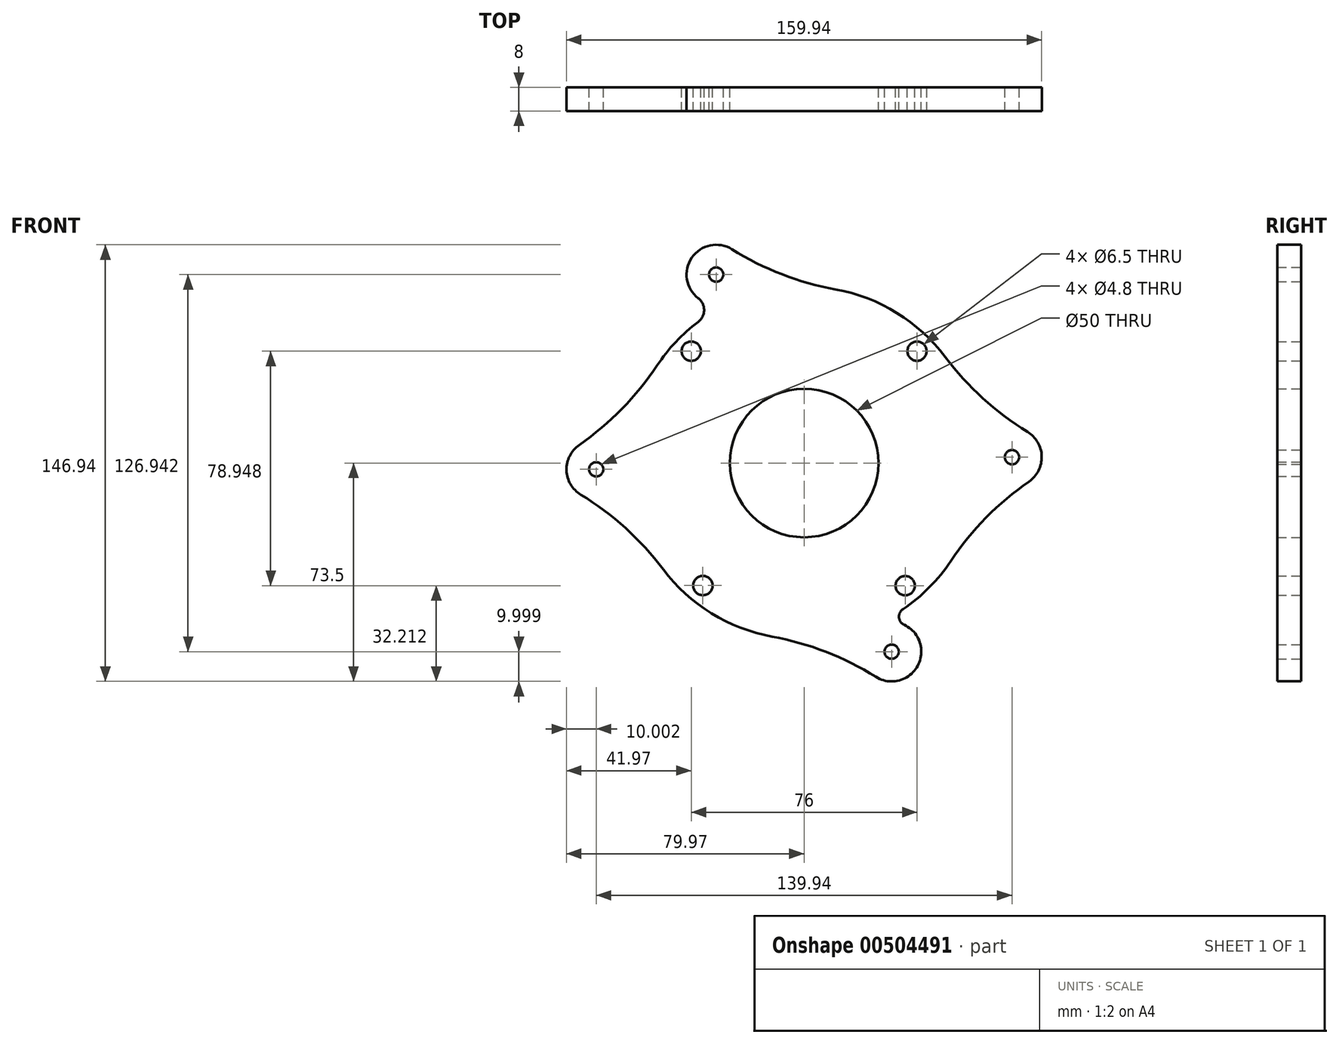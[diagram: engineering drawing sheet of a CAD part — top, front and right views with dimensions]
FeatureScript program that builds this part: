
annotation { "Feature Type Name" : "Feature", "Feature Type Description" : "" }
export const myFeature = defineFeature(function(context is Context, id is Id, definition is map)
    precondition{}
    {
        {
            var Q0;
            Q0=qCreatedBy(makeId("Front.planeOp"),FACE);
            var sketch = newSketch(context, id + "F0", { "sketchPlane" : qUnion([Q0])});
            skArc(sketch, "E0", {"start": v(-35.66, 47.5) * mm, "mid": v(-43.2, 40.77) * mm, "end": v(-49.48, 32.86) * mm});
            skCircle(sketch, "E1", {"center": v(0, 0) * mm, "radius": 53.5 * mm, "construction": true});
            skCircle(sketch, "E2", {"center": v(0, 0) * mm, "radius": 70 * mm, "construction": true});
            skCircle(sketch, "E3", {"center": v(0, 0) * mm, "radius": 80 * mm, "construction": true});
            skCircle(sketch, "E4", {"center": v(0, 0) * mm, "radius": 25 * mm});
            skCircle(sketch, "E5", {"center": v(-38, 37.66) * mm, "radius": 3.25 * mm});
            skCircle(sketch, "E6", {"center": v(38, 37.66) * mm, "radius": 3.25 * mm});
            skCircle(sketch, "E7", {"center": v(34.02, -41.29) * mm, "radius": 3.25 * mm});
            skCircle(sketch, "E8", {"center": v(-34.08, -41.24) * mm, "radius": 3.25 * mm});
            skCircle(sketch, "E9", {"center": v(-29.58, 63.44) * mm, "radius": 2.4 * mm});
            skCircle(sketch, "E10", {"center": v(69.97, 1.98) * mm, "radius": 2.4 * mm});
            skCircle(sketch, "E11", {"center": v(29.46, -63.5) * mm, "radius": 2.4 * mm});
            skCircle(sketch, "E12", {"center": v(-69.97, -2.12) * mm, "radius": 2.4 * mm});
            skLineSegment(sketch, "E13", {"start": v(-29.58, 63.44) * mm, "end": v(0, 0) * mm, "construction": true});
            skArc(sketch, "E14", {"start": v(-24.3, 71.93) * mm, "mid": v(-37.82, 69.12) * mm, "end": v(-35.64, 55.48) * mm});
            skArc(sketch, "E15", {"start": v(-75.68, 6.1) * mm, "mid": v(-79.96, -2.42) * mm, "end": v(-75.17, -10.66) * mm});
            skArc(sketch, "E16", {"start": v(24.15, -71.98) * mm, "mid": v(38.25, -68.27) * mm, "end": v(33.67, -54.43) * mm});
            skArc(sketch, "E17", {"start": v(75.67, -6.24) * mm, "mid": v(79.97, 2.26) * mm, "end": v(75.2, 10.5) * mm});
            skArc(sketch, "E18", {"start": v(47.48, 35.7) * mm, "mid": v(60.14, 21.8) * mm, "end": v(75.2, 10.5) * mm});
            skArc(sketch, "E19", {"start": v(75.67, -6.24) * mm, "mid": v(61.28, -18.36) * mm, "end": v(49.42, -32.96) * mm});
            skArc(sketch, "E20", {"start": v(-24.3, 71.93) * mm, "mid": v(-7.47, 63.53) * mm, "end": v(10.64, 58.44) * mm});
            skArc(sketch, "E21", {"start": v(-35.66, 47.5) * mm, "mid": v(-33.66, 51.49) * mm, "end": v(-35.64, 55.48) * mm});
            skArc(sketch, "E22", {"start": v(-47.4, -35.8) * mm, "mid": v(-60.1, -21.91) * mm, "end": v(-75.17, -10.66) * mm});
            skArc(sketch, "E23", {"start": v(24.15, -71.98) * mm, "mid": v(7.34, -63.55) * mm, "end": v(-10.76, -58.42) * mm});
            skArc(sketch, "E24", {"start": v(33.25, -49.22) * mm, "mid": v(31.94, -51.95) * mm, "end": v(33.67, -54.43) * mm});
            skArc(sketch, "E25", {"start": v(-75.68, 6.1) * mm, "mid": v(-61.32, 18.24) * mm, "end": v(-49.48, 32.86) * mm});
            skArc(sketch, "E26.trimOffspring", {"start": v(47.48, 35.7) * mm, "mid": v(31.2, 50.54) * mm, "end": v(10.64, 58.44) * mm});
            skArc(sketch, "E27.trimOffspring", {"start": v(33.25, -49.22) * mm, "mid": v(42.13, -41.88) * mm, "end": v(49.42, -32.96) * mm});
            skArc(sketch, "E28.trimOffspring", {"start": v(-47.4, -35.8) * mm, "mid": v(-31.2, -50.54) * mm, "end": v(-10.76, -58.42) * mm});
            skSolve(sketch);
        }
        {
            var Q0;
            Q0=makeQuery(id+"F0.imprint","IMPRINT",FACE,{"disambiguationData":[TD([[makeQuery(id+"F0.imprint","IMPRINT",EDGE,{"derivedFrom":sQuery(id+"F0.wireOp",EDGE,"E0")}),1.0]])]});
            extrude(context, id + "F1", {"entities" : qUnion([Q0]), "depth" : 8 * mm});
        }
    });
